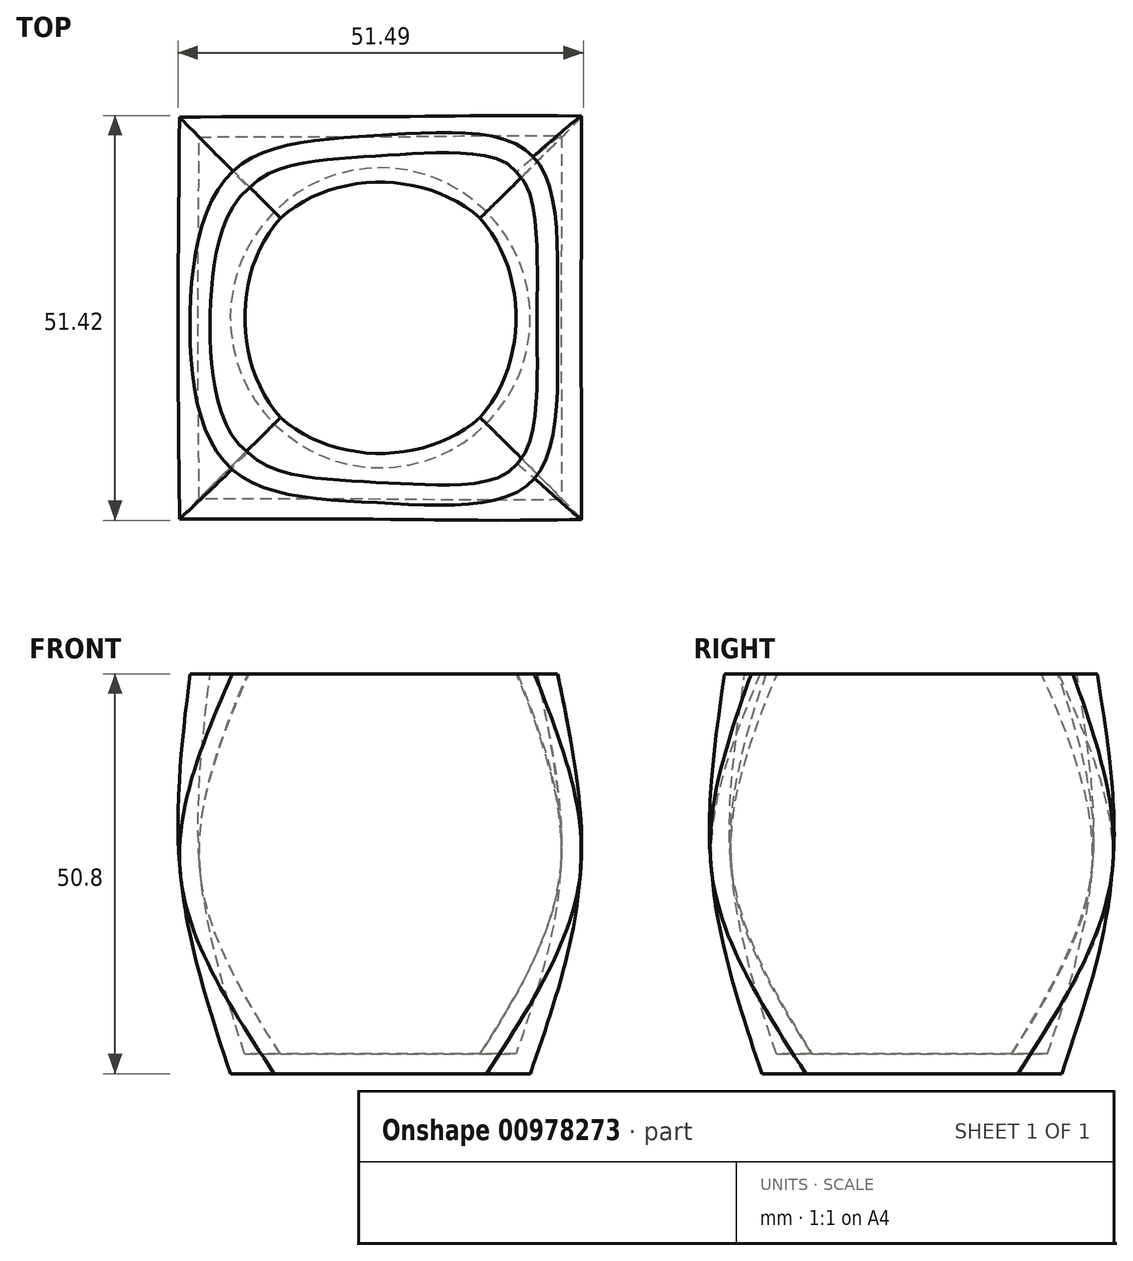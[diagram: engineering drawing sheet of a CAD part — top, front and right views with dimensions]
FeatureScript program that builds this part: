
annotation { "Feature Type Name" : "Feature", "Feature Type Description" : "" }
export const myFeature = defineFeature(function(context is Context, id is Id, definition is map)
    precondition{}
    {
        {
            var Q0;
            Q0=qCreatedBy(makeId("Top.planeOp"),FACE);
            var sketch = newSketch(context, id + "F0", { "sketchPlane" : qUnion([Q0])});
            skCircle(sketch, "E0", {"center": v(0, 0) * mm, "radius": 19.05 * mm});
            skSolve(sketch);
        }
        {
            var Q0;
            Q0=qCreatedBy(makeId("Top.planeOp"),FACE);
            cPlane(context, id + "F1", {"entities" : qUnion([Q0]), "cplaneType" : CPlaneType.OFFSET, "offset" : 25.4 * mm, "width" : 152.4 * mm, "height" : 152.4 * mm});
        }
        {
            var Q0;
            Q0=qCreatedBy(id+"F1.planeOp",FACE);
            var sketch = newSketch(context, id + "F2", { "sketchPlane" : qUnion([Q0])});
            skLineSegment(sketch, "E1.bottom", {"start": v(25.4, -25.4) * mm, "end": v(-25.4, -25.4) * mm});
            skLineSegment(sketch, "E1.top", {"start": v(25.4, 25.4) * mm, "end": v(-25.4, 25.4) * mm});
            skLineSegment(sketch, "E1.left", {"start": v(25.4, -25.4) * mm, "end": v(25.4, 25.4) * mm});
            skLineSegment(sketch, "E1.right", {"start": v(-25.4, -25.4) * mm, "end": v(-25.4, 25.4) * mm});
            skPoint(sketch, "E1.middle", {"position": v(0, 0) * mm});
            skSolve(sketch);
        }
        {
            var Q0;
            Q0=qCreatedBy(id+"F1.planeOp",FACE);
            cPlane(context, id + "F3", {"entities" : qUnion([Q0]), "cplaneType" : CPlaneType.OFFSET, "offset" : 25.4 * mm, "width" : 152.4 * mm, "height" : 152.4 * mm});
        }
        {
            var Q0;
            Q0=qCreatedBy(id+"F3.planeOp",FACE);
            var sketch = newSketch(context, id + "F4", { "sketchPlane" : qUnion([Q0])});
            skFitSpline(sketch, "E2", {"points": [v(0, 23.17) * mm, v(-18.61, 18.72) * mm, v(-24.17, 0) * mm, v(-19.06, -19.06) * mm, v(0, -23.5) * mm, v(19.17, -20.84) * mm, v(22.5, 0) * mm, v(19.17, 20.72) * mm, v(0, 23.17) * mm]});
            skSolve(sketch);
        }
        {
            var Q0;
            Q0=makeQuery(id+"F4.imprint","IMPRINT",FACE,{"disambiguationData":[TD([[makeQuery(id+"F4.imprint","IMPRINT",EDGE,{"derivedFrom":sQuery(id+"F4.wireOp",EDGE,"E2")}),1.0]])]});
            var Q1;
            Q1=makeQuery(id+"F2.imprint","IMPRINT",FACE,{"disambiguationData":[TD([[makeQuery(id+"F2.imprint","IMPRINT",EDGE,{"derivedFrom":sQuery(id+"F2.wireOp",EDGE,"E1.bottom")}),-1.0]])]});
            var Q2;
            Q2=makeQuery(id+"F0.imprint","IMPRINT",FACE,{"disambiguationData":[TD([[makeQuery(id+"F0.imprint","IMPRINT",EDGE,{"derivedFrom":sQuery(id+"F0.wireOp",EDGE,"E0")}),1.0]])]});
            loft(context, id + "F5", {"sheetProfilesArray" : [{ "sheetProfileEntities" : qUnion([Q0]) }, { "sheetProfileEntities" : qUnion([Q1]) }, { "sheetProfileEntities" : qUnion([Q2]) }]});
        }
        {
            var Q0;
            Q0=makeQuery(id+"F5.opLoft","CAP_FACE",FACE,{"disambiguationData":[OSD([makeQuery(id+"F4.imprint","IMPRINT",FACE,{"disambiguationData":[TD([[makeQuery(id+"F4.imprint","IMPRINT",EDGE,{"derivedFrom":sQuery(id+"F4.wireOp",EDGE,"E2")}),1.0]])]})])],"isStart":true});
            shell(context, id + "F6", {"entities" : qUnion([Q0]), "thickness" : 2.54 * mm});
        }
    });
